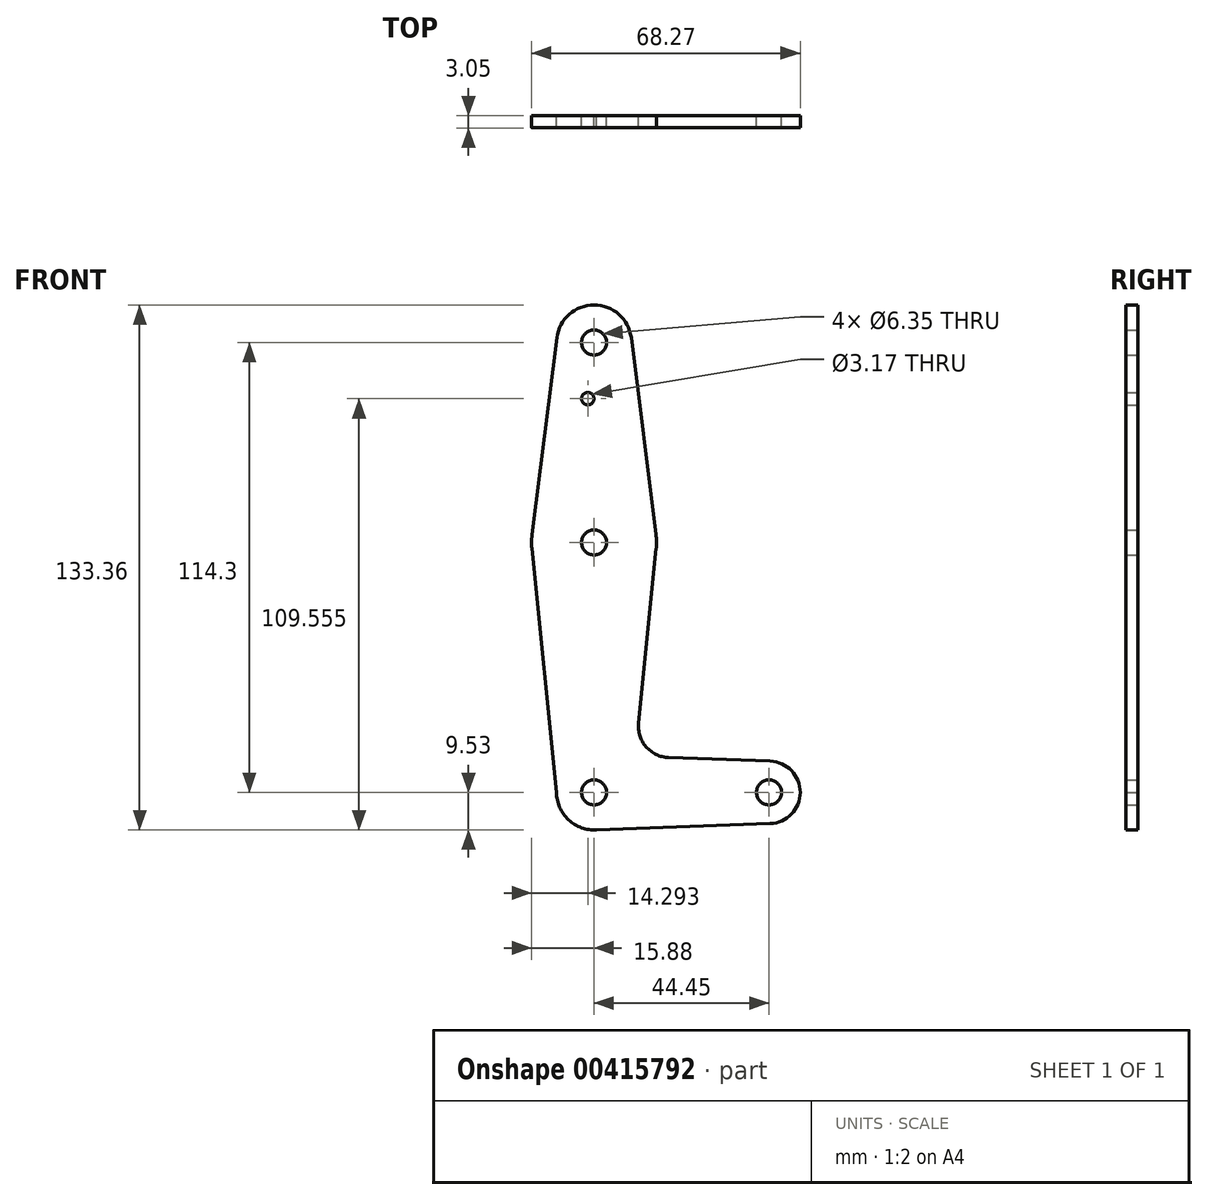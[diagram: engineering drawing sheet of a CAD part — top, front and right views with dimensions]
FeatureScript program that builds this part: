
annotation { "Feature Type Name" : "Feature", "Feature Type Description" : "" }
export const myFeature = defineFeature(function(context is Context, id is Id, definition is map)
    precondition{}
    {
        {
            var Q0;
            Q0=qCreatedBy(makeId("Front.planeOp"),FACE);
            var sketch = newSketch(context, id + "F0", { "sketchPlane" : qUnion([Q0])});
            skLineSegment(sketch, "E0", {"start": v(0, 0) * mm, "end": v(0, 114.3) * mm});
            skLineSegment(sketch, "E1", {"start": v(0, 114.3) * mm, "end": v(0, 0) * mm, "construction": true});
            skLineSegment(sketch, "E2", {"start": v(0, 0) * mm, "end": v(44.45, 0) * mm, "construction": true});
            skCircle(sketch, "E3", {"center": v(0, 114.3) * mm, "radius": 9.53 * mm});
            skCircle(sketch, "E4", {"center": v(0, 63.5) * mm, "radius": 15.88 * mm});
            skCircle(sketch, "E5", {"center": v(0, 0) * mm, "radius": 9.53 * mm});
            skCircle(sketch, "E6", {"center": v(44.45, 0) * mm, "radius": 7.94 * mm});
            skLineSegment(sketch, "E7", {"start": v(-9.45, 115.5) * mm, "end": v(-15.75, 65.48) * mm});
            skLineSegment(sketch, "E8", {"start": v(9.45, 115.5) * mm, "end": v(15.75, 65.48) * mm});
            skLineSegment(sketch, "E9", {"start": v(-15.8, 61.91) * mm, "end": v(-9.52, 0) * mm});
            skLineSegment(sketch, "E10", {"start": v(15.8, 61.9) * mm, "end": v(11.3, 17.6) * mm});
            skLineSegment(sketch, "E11", {"start": v(0, -9.53) * mm, "end": v(44.73, -7.93) * mm});
            skLineSegment(sketch, "E12", {"start": v(18.93, 8.85) * mm, "end": v(44.73, 7.93) * mm});
            skCircle(sketch, "E13", {"center": v(0, 114.3) * mm, "radius": 3.18 * mm});
            skCircle(sketch, "E14", {"center": v(0, 63.5) * mm, "radius": 3.18 * mm});
            skCircle(sketch, "E15", {"center": v(0, 0) * mm, "radius": 3.18 * mm});
            skCircle(sketch, "E16", {"center": v(44.45, 0) * mm, "radius": 3.18 * mm});
            skCircle(sketch, "E17", {"center": v(-1.59, 100.03) * mm, "radius": 1.59 * mm});
            skArc(sketch, "E18.filletArc", {"start": v(11.3, 17.6) * mm, "mid": v(13.22, 11.57) * mm, "end": v(18.93, 8.85) * mm});
            skSolve(sketch);
        }
        {
            var Q0;
            Q0 = qSketchRegion(id + "F0", true);
            extrude(context, id + "F1", {"entities" : qUnion([Q0]), "depth" : 3.05 * mm});
        }
    });
